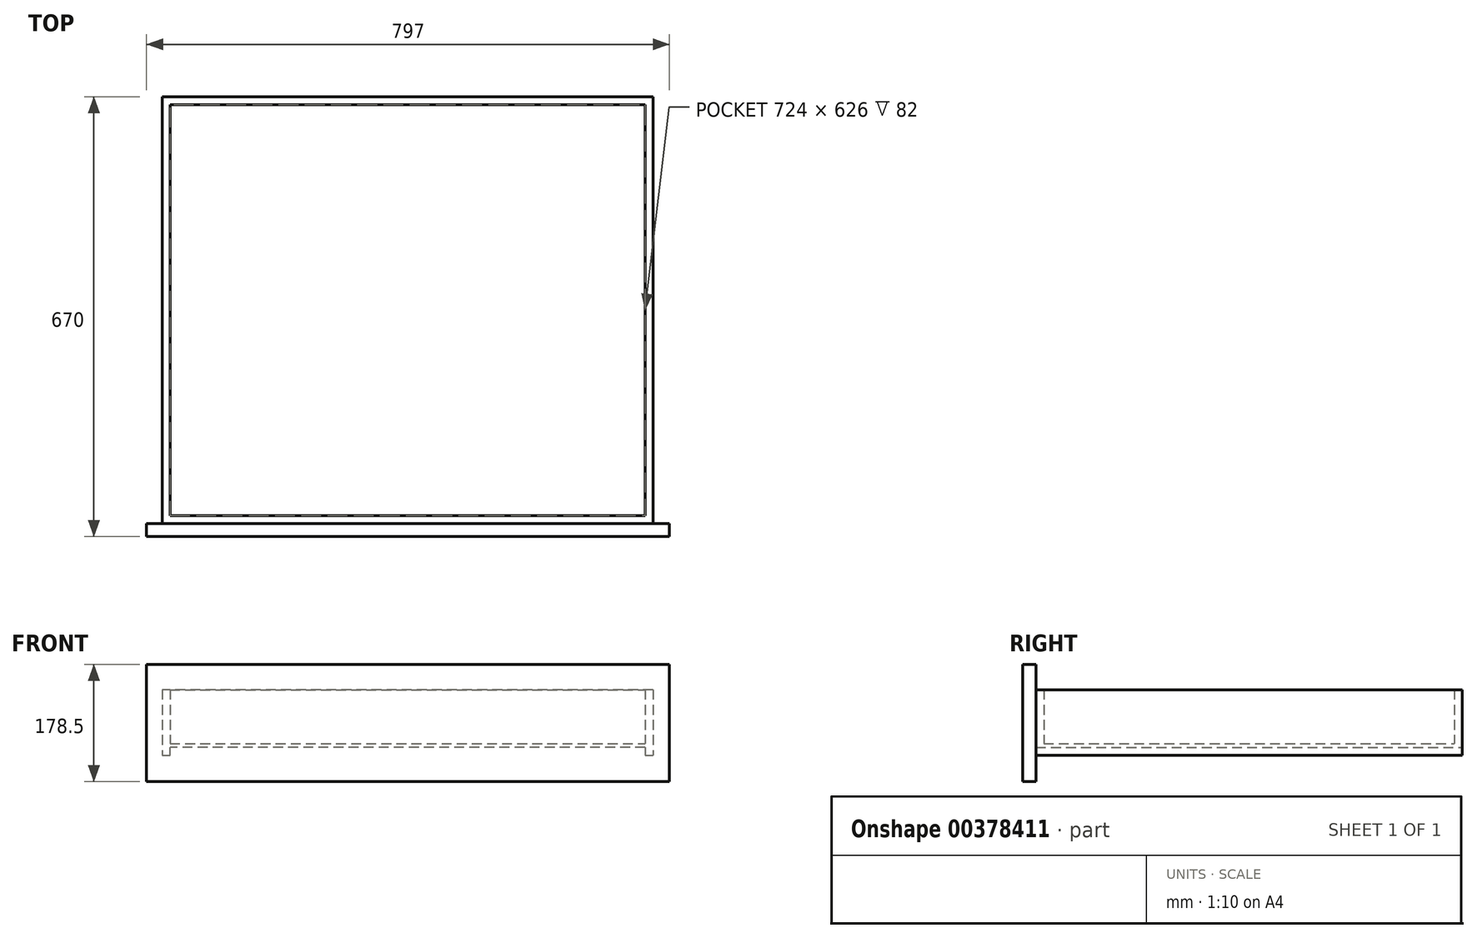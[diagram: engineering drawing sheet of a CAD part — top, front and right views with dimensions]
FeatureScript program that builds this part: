
annotation { "Feature Type Name" : "Feature", "Feature Type Description" : "" }
export const myFeature = defineFeature(function(context is Context, id is Id, definition is map)
    precondition{}
    {
        {
            var Q0;
            Q0=qCreatedBy(makeId("Front.planeOp"),FACE);
            var sketch = newSketch(context, id + "F0", { "sketchPlane" : qUnion([Q0])});
            skLineSegment(sketch, "E0.bottom", {"start": v(362, 3) * mm, "end": v(-362, 3) * mm});
            skLineSegment(sketch, "E0.top", {"start": v(362, -3) * mm, "end": v(-362, -3) * mm});
            skLineSegment(sketch, "E0.left", {"start": v(362, 3) * mm, "end": v(362, -3) * mm});
            skLineSegment(sketch, "E0.right", {"start": v(-362, 3) * mm, "end": v(-362, -3) * mm});
            skPoint(sketch, "E0.middle", {"position": v(0, 0) * mm});
            skLineSegment(sketch, "E1", {"start": v(-362, 3) * mm, "end": v(-362, 85) * mm});
            skLineSegment(sketch, "E2", {"start": v(-362, 85) * mm, "end": v(-374, 85) * mm});
            skLineSegment(sketch, "E3", {"start": v(-374, 85) * mm, "end": v(-374, -15) * mm});
            skLineSegment(sketch, "E4", {"start": v(-374, -15) * mm, "end": v(-362, -15) * mm});
            skLineSegment(sketch, "E5", {"start": v(-362, -15) * mm, "end": v(-362, -3) * mm});
            skLineSegment(sketch, "E6.bottom", {"start": v(362, 85) * mm, "end": v(374, 85) * mm});
            skLineSegment(sketch, "E6.top", {"start": v(362, -15) * mm, "end": v(374, -15) * mm});
            skLineSegment(sketch, "E6.left", {"start": v(362, 85) * mm, "end": v(362, -15) * mm});
            skLineSegment(sketch, "E6.right", {"start": v(374, 85) * mm, "end": v(374, -15) * mm});
            skSolve(sketch);
        }
        {
            var Q0;
            Q0 = qSketchRegion(id + "F0", true);
            extrude(context, id + "F1", {"entities" : qUnion([Q0]), "depth" : 650 * mm});
        }
        {
            var Q0;
            {var subQ0=sQuery(id+"F0.wireOp",EDGE,"E6.left");Q0=makeQuery(id+"F1.opExtrude","SWEPT_FACE",FACE,{"disambiguationData":[OSD([subQ0]),TDD([makeQuery(id+"F0.imprint","IMPRINT",EDGE,{"disambiguationData":[TD([[makeQuery(id+"F0.imprint","INTERSECT",VERTEX,{"derivedFrom":[sQuery(id+"F0.wireOp",EDGE,"E0.bottom"),subQ0]}),1.0]])],"derivedFrom":subQ0})])]});}
            var sketch = newSketch(context, id + "F2", { "sketchPlane" : qUnion([Q0])});
            skLineSegment(sketch, "E7.bottom", {"start": v(0, 85) * mm, "end": v(12, 85) * mm});
            skLineSegment(sketch, "E7.top", {"start": v(0, 3) * mm, "end": v(12, 3) * mm});
            skLineSegment(sketch, "E7.left", {"start": v(0, 85) * mm, "end": v(0, 3) * mm});
            skLineSegment(sketch, "E7.right", {"start": v(12, 85) * mm, "end": v(12, 3) * mm});
            skLineSegment(sketch, "E8.bottom", {"start": v(650, 85) * mm, "end": v(638, 85) * mm});
            skLineSegment(sketch, "E8.top", {"start": v(650, 3) * mm, "end": v(638, 3) * mm});
            skLineSegment(sketch, "E8.left", {"start": v(650, 85) * mm, "end": v(650, 3) * mm});
            skLineSegment(sketch, "E8.right", {"start": v(638, 85) * mm, "end": v(638, 3) * mm});
            skSolve(sketch);
        }
        {
            var Q0;
            Q0 = qSketchRegion(id + "F2", true);
            extrude(context, id + "F3", {"entities" : qUnion([Q0]), "operationType" : NewBodyOperationType.ADD, "depth" : 724 * mm});
        }
        {
            var Q0;
            Q0=makeQuery(id+"F3.boolean.opBoolean","MERGE",FACE,{"derivedFrom":[makeQuery(id+"F1.opExtrude","CAP_FACE",FACE,{"disambiguationData":[OSD([sQuery(id+"F0.wireOp",EDGE,"E0.bottom"),sQuery(id+"F0.wireOp",EDGE,"E0.top"),sQuery(id+"F0.wireOp",EDGE,"E1"),sQuery(id+"F0.wireOp",EDGE,"E2"),sQuery(id+"F0.wireOp",EDGE,"E3"),sQuery(id+"F0.wireOp",EDGE,"E4"),sQuery(id+"F0.wireOp",EDGE,"E5"),sQuery(id+"F0.wireOp",EDGE,"E6.bottom"),sQuery(id+"F0.wireOp",EDGE,"E6.top"),sQuery(id+"F0.wireOp",EDGE,"E6.left"),sQuery(id+"F0.wireOp",EDGE,"E6.right")])],"isStart":false}),makeQuery(id+"F3.opExtrude","SWEPT_FACE",FACE,{"disambiguationData":[OSD([sQuery(id+"F2.wireOp",EDGE,"E8.left")])]})]});
            var sketch = newSketch(context, id + "F4", { "sketchPlane" : qUnion([Q0])});
            skLineSegment(sketch, "E9.bottom", {"start": v(-398, 123.5) * mm, "end": v(399, 123.5) * mm});
            skLineSegment(sketch, "E9.top", {"start": v(-398, -55) * mm, "end": v(399, -55) * mm});
            skLineSegment(sketch, "E9.left", {"start": v(-398, 123.5) * mm, "end": v(-398, -55) * mm});
            skLineSegment(sketch, "E9.right", {"start": v(399, 123.5) * mm, "end": v(399, -55) * mm});
            skSolve(sketch);
        }
        {
            var Q0;
            Q0 = qSketchRegion(id + "F4", true);
            extrude(context, id + "F5", {"entities" : qUnion([Q0]), "operationType" : NewBodyOperationType.ADD, "depth" : 20 * mm});
        }
    });
